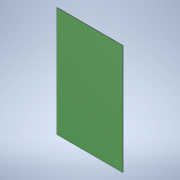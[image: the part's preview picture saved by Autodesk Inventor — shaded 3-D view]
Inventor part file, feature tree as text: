
AUTODESK INVENTOR PART (.ipt)
format: ipt  version: 2020.2 (Build 242310000, 310)  size: 94,720 bytes
history: native  units: mm
features: extrude x1, sketch x1
ambient origin geometry x8: Origin, YZ Plane, XZ Plane, XY Plane, X Axis, Y Axis, Z Axis, Center Point
bodies: Solid1 (feature_tree)
feature tree (2):
  extrude  "Extrusion1"  Depth=500.0mm
  sketch  "Sketch1"  dims[d0=300.0mm d1=500.0mm d2=2.0mm d3=0.0mm]
